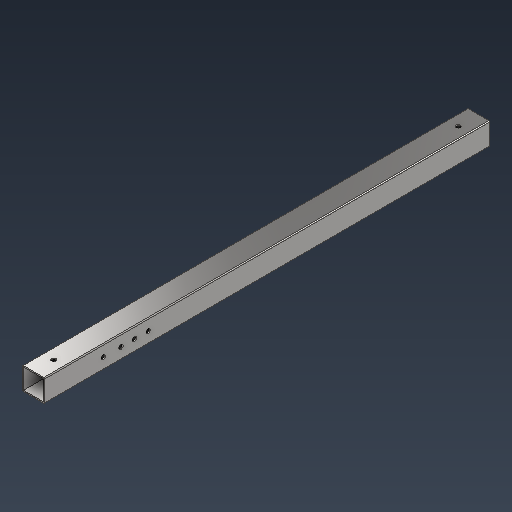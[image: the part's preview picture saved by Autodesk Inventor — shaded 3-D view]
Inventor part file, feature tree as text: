
AUTODESK INVENTOR PART (.ipt)
format: ipt  version: 2021 (Build 250183000, 183)  size: 190,976 bytes
history: native  units: mm
features: sketch x4, hole x3, extrude x1, fillet x1
ambient origin geometry x8: Origin, YZ Plane, XZ Plane, XY Plane, X Axis, Y Axis, Z Axis, Center Point
bodies: Solid1 (feature_tree)
feature tree (9):
  sketch  "Sketch1"  dims[d0=50.0mm d1=50.0mm d2=25.0mm]
  extrude  "Extrusion1"  Depth=50.0mm
  fillet  "Fillet1"  Radius=25.0mm
  hole  "endHoles"  [1 undecoded]
  hole  "clampHoles"  [1 undecoded]
  hole  "Hole3"  [1 undecoded]
  sketch  "Sketch2"  dims[d3=25.0mm d4=2.5mm]
  sketch  "Sketch3"  dims[d5=990.0mm d6=0.0mm]
  sketch  "Sketch4"  dims[d7=2.0mm d8=45.0mm d9=0.0mm d10=45.0mm d11=0.0mm d12=10.0mm d13=6.0mm d14=4.0mm d15=2.0mm d16=90.0deg d17=8.0mm d18=0.0mm d19=860.0mm d20=760.0mm d21=0.0mm d22=0.0mm d23=10.0mm d24=6.0mm d25=4.0mm d26=2.0mm d27=90.0deg d28=8.0mm d29=20.594885mm d30=30.0mm d32=39.6mm d33=10.0mm d34=6.0mm d35=4.0mm d36=2.0mm d37=90.0deg d38=8.0mm d39=20.594885mm]
note: 3 required parameter values undecoded (feature->parameter linkage not recoverable at this tier; creation-order binding heuristic only, values carry confidence <= 0.55)
